# Revit family: Bottle Filling Station_Mechanical_Bi-Level-Elkay-EZVRSM-EDFPV_M217D1LK_217D1LK
name_source: partatom
category: Plumbing Fixtures
units: mm (PartAtom-declared; Revit-internal decimal feet)

## family parameters
Cut with Voids When Loaded = No
Host = Face
Maintain Annotation Orientation = No
OmniClass Number = 23.65.70.14.11
OmniClass Title = Drinking Fountains/Coolers
Part Type = Normal
Room Calculation Point = No
Round Connector Dimension = Use Diameter
Shared = No

## types (2) — shared parameters
Activation Method = Mechanical Bottle Filler Button with Mechanical Front Bubbler Button
Approx. Shipping Weight (lbs) = 118
Assembly Code = D2010810
Default Elevation = 48 "
Height = 34.63 "
Inlet Connection = 0.38 "
Length = 38.5 "
Manufacturer = (Elkay Manufacturer Company)
Manufacturer Brand = Elkay (by Zurn Elkay Water Solutions)
Material = Finish-Elkay-Stainless Steel
Mounting plate = 12 "
Product Documentation Link = https://www.elkayfiles.com
Product Installation Sheet URL = https://www.elkayfiles.com
Product Page URL = https://www.elkay.com
Repair Parts URL = https://www.elkayfiles.com
Secondary Material = Elkay-Transparent
URL = https://www.elkay.com
Water Outlet connection = 21.5 "
Water Supply Connection = 16.5 "
Width = 19.38 "
zero-valued in all types: Product Weight (lbs)

## per-type parameters (varying)
| type | Description | Model | Outlet Connection |
| EZVRSM-EDFPVM217D1LK (Vandal Resistant Mechanical Bottle Filling Station) | Elkay ezH2O Vandal Resistant Mechanical Bottle Filling Station with Bi-Level Integral Soft Sides® Fountain Non-Filtered Non Refrigerated Stainless | EZVRSM-EDFPVM217D1LK | 1.5 " |
| EZVRSM-EDFPV217D1LK (Vandal Resistant Mechanical Bottle Filling Station) | Elkay ezH2O Vandal Resistant Mechanical Bottle Filling Station with Bi-Level Integral Soft Sides® Fountain Non-Filtered Non-Refrigerated Stainless | EZVRSM-EDFPV217D1LK | 1.25 " |

## geometry (parser evidence)
native form markers: Sweep x35
no freeform markers — native parametric forms only
